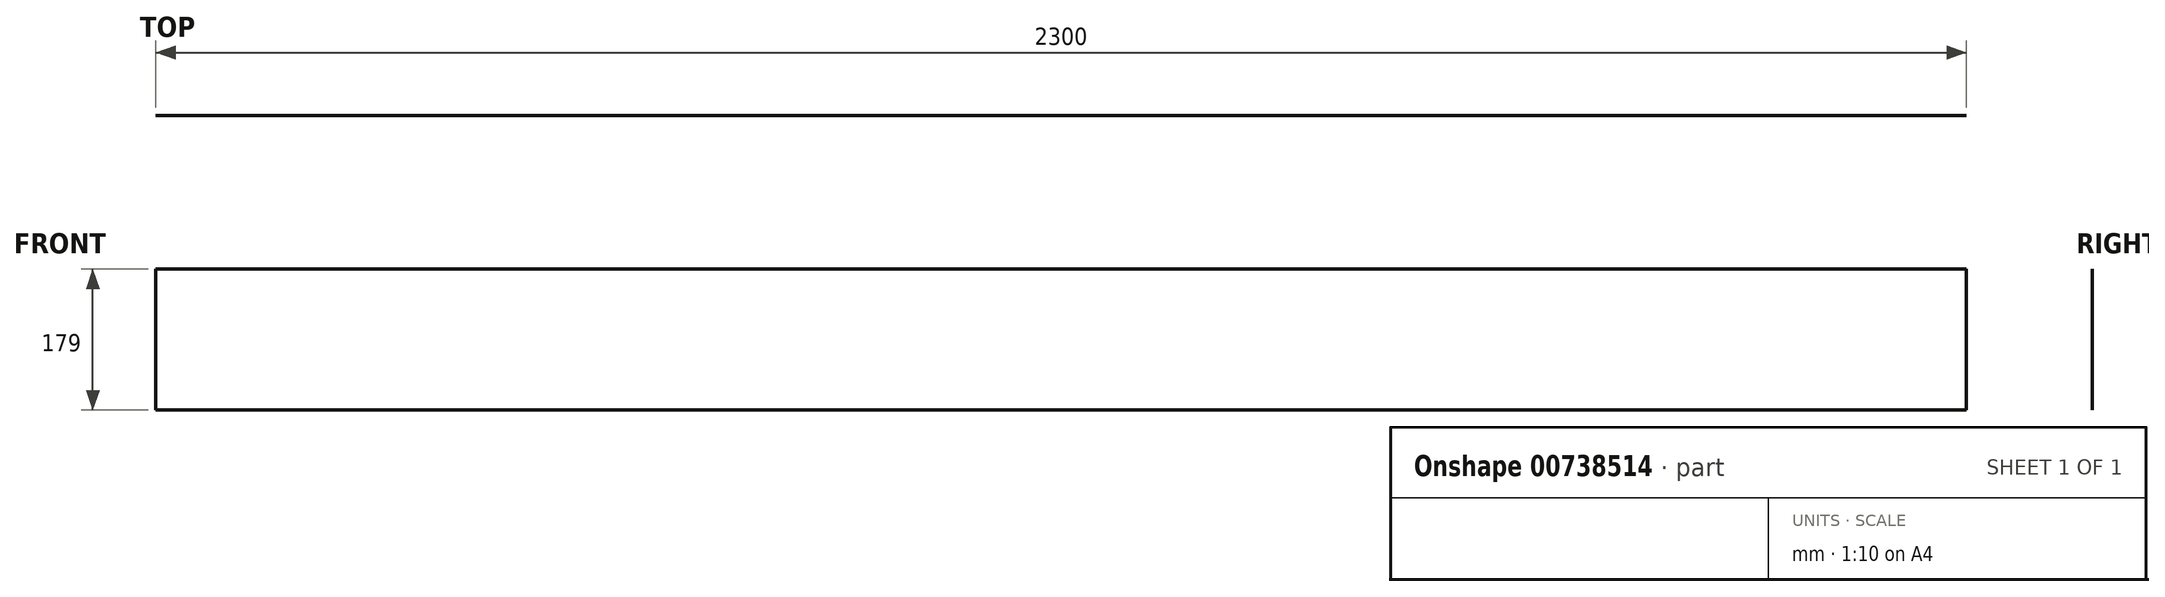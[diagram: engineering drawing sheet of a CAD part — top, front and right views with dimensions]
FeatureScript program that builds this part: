
annotation { "Feature Type Name" : "Feature", "Feature Type Description" : "" }
export const myFeature = defineFeature(function(context is Context, id is Id, definition is map)
    precondition{}
    {
        {
            var Q0;
            Q0=qCreatedBy(makeId("Top.planeOp"),FACE);
            var sketch = newSketch(context, id + "F0", { "sketchPlane" : qUnion([Q0])});
            skLineSegment(sketch, "E0.bottom", {"start": v(-1150, 1065) * mm, "end": v(1150, 1065) * mm});
            skLineSegment(sketch, "E0.top", {"start": v(-1150, -1065) * mm, "end": v(1150, -1065) * mm});
            skLineSegment(sketch, "E0.left", {"start": v(-1150, 1065) * mm, "end": v(-1150, -1065) * mm});
            skLineSegment(sketch, "E0.right", {"start": v(1150, 1065) * mm, "end": v(1150, -1065) * mm});
            skPoint(sketch, "E0.middle", {"position": v(0, 0) * mm});
            skSolve(sketch);
        }
        {
            var Q0;
            Q0=makeQuery(id+"F0.imprint","IMPRINT",FACE,{"disambiguationData":[TD([[makeQuery(id+"F0.imprint","IMPRINT",EDGE,{"derivedFrom":sQuery(id+"F0.wireOp",EDGE,"E0.bottom")}),-1.0]])]});
            var sketch = newSketch(context, id + "F1", { "sketchPlane" : qUnion([Q0])});
            skLineSegment(sketch, "E1.bottom", {"start": v(-1150, 1065) * mm, "end": v(1150, 1065) * mm});
            skLineSegment(sketch, "E1.top", {"start": v(-1150, 1018) * mm, "end": v(1150, 1018) * mm});
            skLineSegment(sketch, "E1.left", {"start": v(-1150, 1065) * mm, "end": v(-1150, 1018) * mm});
            skLineSegment(sketch, "E1.right", {"start": v(1150, 1065) * mm, "end": v(1150, 1018) * mm});
            skLineSegment(sketch, "E2.bottom", {"start": v(-1150, -1065) * mm, "end": v(1150, -1065) * mm});
            skLineSegment(sketch, "E2.top", {"start": v(-1103, -1018) * mm, "end": v(-653, -1018) * mm});
            skLineSegment(sketch, "E2.left", {"start": v(-1150, -1065) * mm, "end": v(-1150, -1041.5) * mm});
            skLineSegment(sketch, "E2.right", {"start": v(1150, -1065) * mm, "end": v(1150, -1041.5) * mm});
            skLineSegment(sketch, "E3", {"start": v(-1103, -1018) * mm, "end": v(-1103, -1041.5) * mm});
            skLineSegment(sketch, "E4", {"start": v(-1103, -1041.5) * mm, "end": v(-1150, -1041.5) * mm});
            skLineSegment(sketch, "E5", {"start": v(-653, -1018) * mm, "end": v(-653, -1041.5) * mm});
            skLineSegment(sketch, "E6", {"start": v(-653, -1041.5) * mm, "end": v(-606, -1041.5) * mm});
            skLineSegment(sketch, "E7", {"start": v(-606, -1041.5) * mm, "end": v(-606, -1018) * mm});
            skLineSegment(sketch, "E8", {"start": v(-606, -1018) * mm, "end": v(-156, -1018) * mm});
            skLineSegment(sketch, "E9", {"start": v(-156, -1018) * mm, "end": v(-156, -1041.5) * mm});
            skLineSegment(sketch, "E10", {"start": v(-156, -1041.5) * mm, "end": v(-109, -1041.5) * mm});
            skLineSegment(sketch, "E11", {"start": v(-109, -1041.5) * mm, "end": v(-109, -1018) * mm});
            skLineSegment(sketch, "E12", {"start": v(341, -1018) * mm, "end": v(341, -1041.5) * mm});
            skLineSegment(sketch, "E13", {"start": v(341, -1041.5) * mm, "end": v(388, -1041.5) * mm});
            skLineSegment(sketch, "E14", {"start": v(388, -1041.5) * mm, "end": v(388, -1018) * mm});
            skLineSegment(sketch, "E15.trimOffspring", {"start": v(-109, -1018) * mm, "end": v(341, -1018) * mm});
            skLineSegment(sketch, "E16.trimOffspring", {"start": v(388, -1018) * mm, "end": v(745.5, -1018) * mm});
            skPoint(sketch, "E17.orphan", {"position": v(-1150, -1018) * mm});
            skLineSegment(sketch, "E18", {"start": v(1103, -1018) * mm, "end": v(1103, -1041.5) * mm});
            skLineSegment(sketch, "E19", {"start": v(1103, -1041.5) * mm, "end": v(1150, -1041.5) * mm});
            skLineSegment(sketch, "E20", {"start": v(745.5, -1018) * mm, "end": v(745.5, -1042.16) * mm});
            skLineSegment(sketch, "E21", {"start": v(745.5, -1042.16) * mm, "end": v(792.5, -1042.16) * mm});
            skLineSegment(sketch, "E22", {"start": v(792.5, -1042.16) * mm, "end": v(792.5, -1018) * mm});
            skLineSegment(sketch, "E23.trimOffspring", {"start": v(792.5, -1018) * mm, "end": v(1103, -1018) * mm});
            skLineSegment(sketch, "E24", {"start": v(-1150, -1041.5) * mm, "end": v(-1150, -1065) * mm});
            skSolve(sketch);
        }
        {
            var Q0;
            Q0=sQuery(id+"F1.wireOp",EDGE,"E2.bottom");
            extrude(context, id + "F2", {"bodyType" : ToolBodyType.SURFACE, "surfaceEntities" : qUnion([Q0]), "depth" : 179 * mm, "offsetDistance" : 25 * mm});
        }
    });
